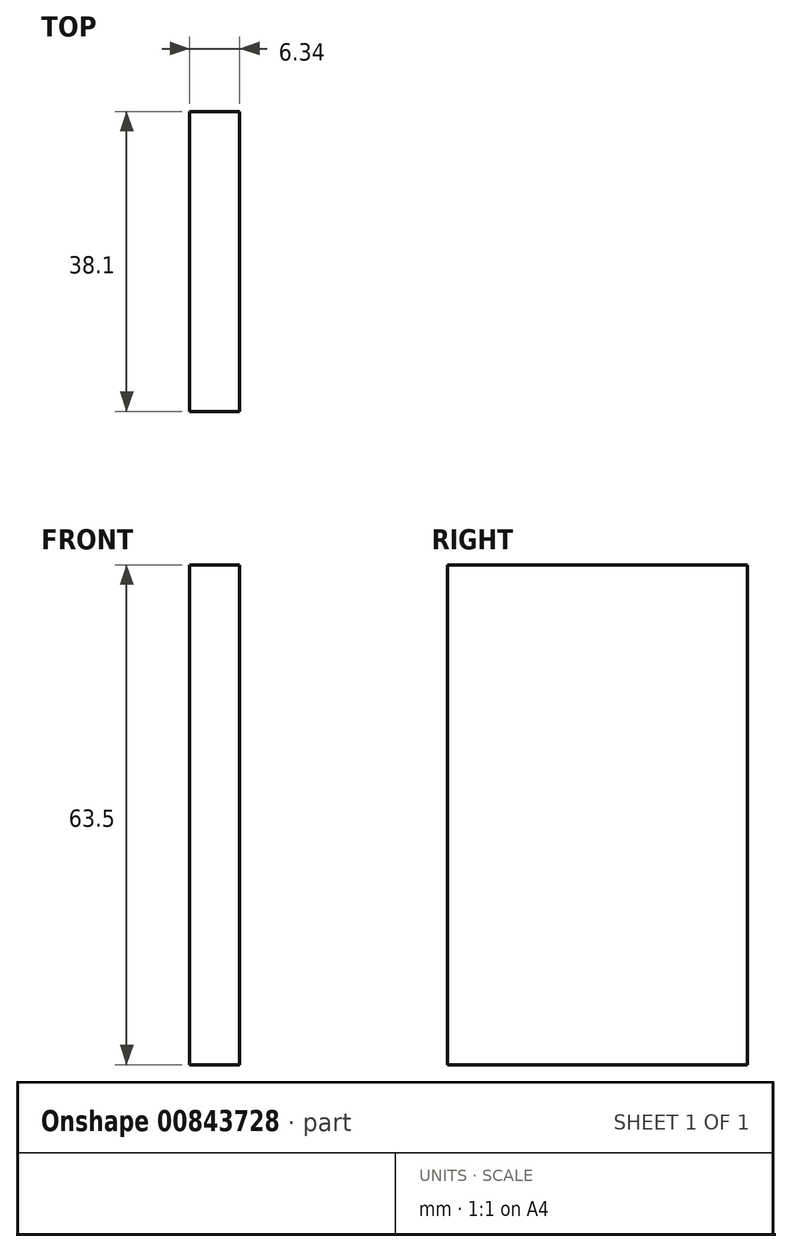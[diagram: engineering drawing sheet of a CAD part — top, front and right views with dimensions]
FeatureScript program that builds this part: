
annotation { "Feature Type Name" : "Feature", "Feature Type Description" : "" }
export const myFeature = defineFeature(function(context is Context, id is Id, definition is map)
    precondition{}
    {
        {
            var Q0;
            Q0=qCreatedBy(makeId("Front.planeOp"),FACE);
            var sketch = newSketch(context, id + "F0", { "sketchPlane" : qUnion([Q0])});
            skLineSegment(sketch, "E0.bottom", {"start": v(3.17, 31.75) * mm, "end": v(-3.18, 31.75) * mm});
            skLineSegment(sketch, "E0.top", {"start": v(3.17, -31.75) * mm, "end": v(-3.17, -31.75) * mm});
            skLineSegment(sketch, "E0.left", {"start": v(3.17, 31.75) * mm, "end": v(3.17, -31.75) * mm});
            skLineSegment(sketch, "E0.right", {"start": v(-3.18, 31.75) * mm, "end": v(-3.17, -31.75) * mm});
            skPoint(sketch, "E0.middle", {"position": v(0, 0) * mm});
            skSolve(sketch);
        }
        {
            var Q0;
            Q0=qSketchRegion(id+"F0",true);
            extrude(context, id + "F1", {"entities" : qUnion([Q0]), "depth" : 38.1 * mm, "offsetDistance" : 25.4 * mm});
        }
    });
